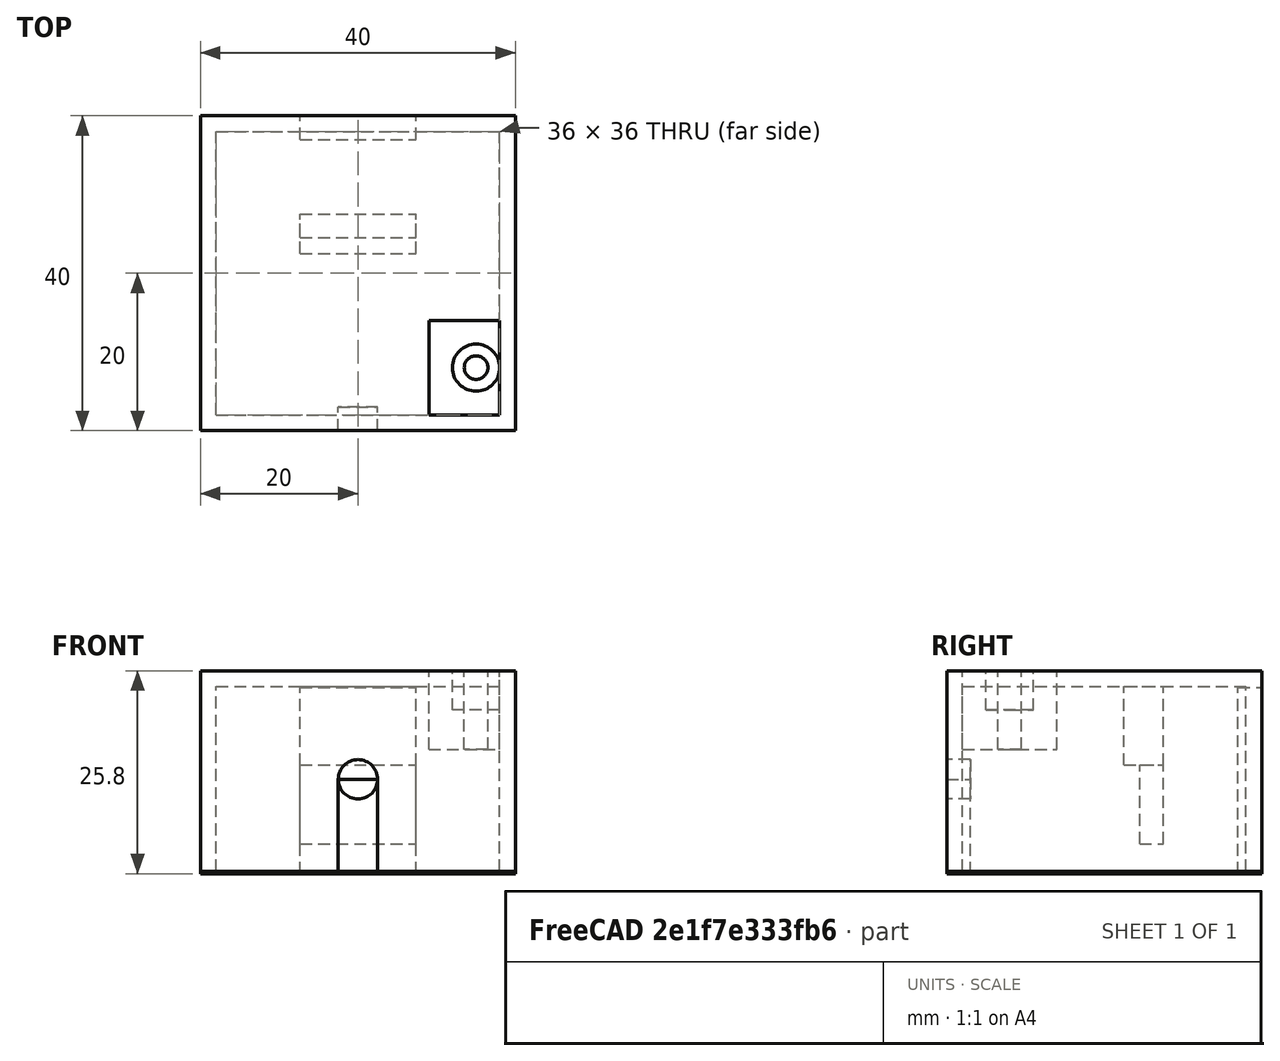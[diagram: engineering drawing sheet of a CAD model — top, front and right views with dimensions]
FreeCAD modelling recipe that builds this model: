
FCSTD DOCUMENT  (FreeCAD 0.19R24291 (Git))
Label: eth_conn_top_1_noncon
License: All rights reserved
LicenseURL: http://en.wikipedia.org/wiki/All_rights_reserved
objects: Part::Box×7, Part::Cylinder×3, Part::Cut×1, Part::Feature×1, Part::Extrusion×1, Surface::GeomFillSurface×1
note: 14 computed .brp shape members not serialized (recipe doc carries the construction recipe); baked Part::Feature solids carry a one-line shape summary decoded from their .brp

FEATURE [Part::Box] Box  label="Cube"
  AttacherType = Attacher::AttachEngine3D
  Height = 25.5
  Length = 40
  Placement = pos=(-20,0,0) rot=(0,0,1;0rad)
  Width = 40
FEATURE [Part::Box] Box001  label="Cube001"
  AttacherType = Attacher::AttachEngine3D
  Height = 23.5
  Length = 36
  Placement = pos=(-18,2,0) rot=(0,0,1;0rad)
  Width = 36
FEATURE [Part::Cut] Cut
  Base = -> Box
  Placement = pos=(0,0,0.3) rot=(0,0,1;0rad)
  Tool = -> Box001
FEATURE [Part::Box] Box002  label="Cube002"
  AttacherType = Attacher::AttachEngine3D
  Height = 12
  Length = 5
  Placement = pos=(-2.5,0,0) rot=(0,0,1;0rad)
  Width = 3
FEATURE [Part::Cylinder] Cylinder
  Angle = 360
  AttacherType = Attacher::AttachEngine3D
  Height = 3
  Placement = pos=(0,3,12) rot=(1,0,0;1.5708rad)
  Radius = 2.5
FEATURE [Part::Box] Box003  label="Cube003"
  AttacherType = Attacher::AttachEngine3D
  Height = 23.7
  Length = 14.7
  Placement = pos=(-7.35,37,0) rot=(0,0,1;0rad)
  Width = 3
FEATURE [Part::Feature] Face
  Placement = pos=(0,0,0.3) rot=(0,0,1;0rad)
  shape: bbox 40 x 40 x 2e-07 mm, 1 faces, 0 solids (baked)
FEATURE [Part::Extrusion] Extrusion
  Base = -> Face
  Dir = (0,0,-0.3)
  DirMode = 0
  FaceMakerClass = Part::FaceMakerBullseye
  LengthFwd = 0
  LengthRev = 0
  Solid = true
  Symmetric = false
FEATURE [Part::Box] Box004  label="Cube004"
  AttacherType = Attacher::AttachEngine3D
  Height = 10
  Length = 14.7
  Placement = pos=(-7.35,22.5,13.8) rot=(0,0,1;0rad)
  Width = 5
FEATURE [Part::Box] Box005  label="Cube005"
  AttacherType = Attacher::AttachEngine3D
  Height = 10
  Length = 14.7
  Placement = pos=(-7.35,24.5,3.8) rot=(0,0,1;0rad)
  Width = 3
FEATURE [Surface::GeomFillSurface] Surface
  BoundaryList = -> [Box004,Box005]
  FillType = 0
FEATURE [Part::Cylinder] Cylinder001
  Angle = 360
  AttacherType = Attacher::AttachEngine3D
  Height = 5
  Placement = pos=(15,8,20.8) rot=(0,0,1;0rad)
  Radius = 3
FEATURE [Part::Box] Box006  label="Cube006"
  AttacherType = Attacher::AttachEngine3D
  Height = 10
  Length = 9
  Placement = pos=(9,2,15.8) rot=(0,0,1;0rad)
  Width = 12
FEATURE [Part::Cylinder] Cylinder002
  Angle = 360
  AttacherType = Attacher::AttachEngine3D
  Height = 10
  Placement = pos=(15,8,15.8) rot=(0,0,1;0rad)
  Radius = 1.5
